# Revit family: IS_Ceraline_A6938_BIM_NL
name_source: partatom
category: Plumbing Fixtures
units: mm (PartAtom-declared; Revit-internal decimal feet)

## family parameters
Always vertical = No
Cut with Voids When Loaded = No
OmniClass Number = 23.45.55.17
OmniClass Title = Mixing Faucets
Part Type = Normal
Room Calculation Point = No
Round Connector Dimension = Use Diameter
Shared = No
Work Plane-Based = No

## types (2) — shared parameters
Accesoires = https://www.idealstandard.nl
Afmetingen = 113 x 213 x 193 mm
AfstandsEenheid = Millimeter
Artikelreferentie = CERALINE WASCHTISCHMISCHER EINBAUKIT2 HORIZ/A1313NU
Auteur = Ideal Standard
BIMObjectName = Washbasin manual water supply sets_Ceraline_A6938AA_Ideal Standard
BIMobject category = Sanitary
BIMobject category code = Sanitary Taps & Mixer
BIMobject main category = Sanitary
BIMobject main category code = sanitary
BOSUseNativeGeometries = 1
Bedieningkraan = Handbuch
Bedieningkraanwerk = einzelne Ebene
Beschrijvinggarantie = Herstellergarantie
BimObjectNaam = Washbasin manual water supply sets_Ceraline_A6938AA_Ideal Standard
Brand url = http://www.idealstandard.nl
Breedte = 193.000002
Date of publishing = 20/05/2019
Diepte = 213 mm  [stored 0.698819 ft]
DikteMateriaal = Messing
Doorstromingscoëfficiënt = 14L/min
Douchebak = No
DuurEenheid = Jaren
Edition number = 1
Features = CERALINE BSN MXR BIN KIT2 H/A5948NU MENA
Functiekraanwerk = Einhebelgriff
Garantieunits = Jaren
GemaaktOp = 22/07/2021
Hoogte = 113.464935302735
Hulp = https://www.idealstandard.nl
IFC Classification = Sanitary Terminal
IfcExportAs = IfcValveType
IfcExportType = FAUCED
Installatieinstructies = https://www.idealstandard.nl
Installation instructions = https://www.idealstandard.nl
Lengte = 213 mm  [stored 0.698819 ft]
Manufacturer name = Ideal Standard
Masterformat 2014 Code = 41 14 33
Masterformat 2014 Description = Mixer
Materiaal = Messing
Material main = Brass
Merk = Ideal Standard
ModelReference = CERALINE BSN MXR BIN KIT2 H/A5948NU MENA
Montageinstuctie = https://www.idealstandard.nl
NBS Reference Code = 45-35-70/371
NBS Reference Description = Washbasin manual water supply sets
Name = IS_IdealStandard_Washbasinmanualwatersupplysets_Ceraline_A6938AA
Nettogewicht = 0.88
NominalHeight = 113 mm
NominalLength = 213 mm  [stored 0.698819 ft]
NominalWidth = 193 mm
Normen = IS_IdealStandard_Washbasinmanualwatersupplysets_Ceraline_A6938AA
OmniClass Code = 23-31 11 00
OmniClass Description = Faucets
OppervlakteEenheid = Millimeter
Product Guid = 513090a8-e12e-4011-8710-158d55a47c0e
Product certification = https://www.idealstandard.nl
Product data url = https://bimobject.com
Product family = Ceraline
Product group = Washbasin manual water supply sets
Product name = CERALINE BSN MXR BIN KIT2 H/A5948NU MENA
Product url = https://www.idealstandard.nl
ProductSoort = Armaturen Mixer
Productinformatie = https://www.idealstandard.nl
QR code = http://bimobject.com
Referentie = CERALINE BSN MXR BIN KIT2 H/A5948NU MENA
Revisie = 1
Size = 113 x 213 x 193 mm
Technical description = https://www.idealstandard.nl
Telefoonnummer = 077 355 08 08
Testdruk = 10 Bar
Typeconnectie = Installation
URL = https://www.idealstandard.nl
Uniclass 2015 Code = Pr_40_20_87_96
Uniclass 2015 Name = Washbasin manual water supply sets
Urlproducent = https://www.idealstandard.nl
ValutaEenheid = Euro
Versie = 1
Volumeunits = Liter
Vorm = zylindrisch
WarrantyDescription = Manufacturers Warranty
WarrantyDurationParts = 5
WarrantyDurationUnit = year
Wisselstukken = https://www.idealstandard.nl
Youtube clip = https://www.youtube.com
zero-valued in all types: BrutoGewicht, Cost, Overloop, Vervangingskosten

## per-type parameters (varying)
| type | Afwerking | Artikelnummer | Artikelomschrijving | BarCode | Barcode | Description | Eigenschappen | Finish | GTIN code | Kleur | Model | ModelNumber | Product SKU | Uniclass 1.4 Code | Uniclass 1.4 Description | Uniclass2015Beschrijving | Uniclass2015Referentie | Uniclass2015Version |
| A6938AA - CERALINE BASIN MIXER BUILT-IN KIT2 HORIZ/A1313NU  - CHROME | chrom | A6938AA | CERALINE WASCHTISCHMISCHER EINBAUKIT2 HORIZ/A1313NU - CHROM | 4015413343879 | 4015413343879 | CERALINE BASIN MIXER BUILT-IN KIT2 HORIZ/A1313NU  - CHROME | WASCHTISCHMISCHER EINBAUKIT2 HORIZ/A1313NU - CHROM | chrom | https://4015413343879 | chrom | A6938AA | A6938AA | A6938AA |  |  |  |  |  |
| A6938XG - CERALINE BASIN MIXER BUILT-IN KIT2 HORIZ/A1313NU  - SILK BLACK | seide schwarz | A6938XG | CERALINE WASCHTISCHMISCHER EINBAUKIT2 HORIZ/A1313NU - SEIDE SCHWARZ | 4015413350884 | 4015413350884 | CERALINE BASIN MIXER BUILT-IN KIT2 HORIZ/A1313NU  - SILK BLACK | WASCHTISCHMISCHER EINBAUKIT2 HORIZ/A1313NU - SEIDE SCHWARZ | seide schwarz | https://4015413350884 | seide schwarz | A6938XG | A6938XG | A6938XG | L725111 | Mixers taps | Washbasin manual water supply sets | Pr_40_20_87_96 | v1.22 |

note: [stored X ft] marks values corroborated as IEEE doubles in the binary element streams (Revit-internal decimal feet)

## geometry (parser evidence)
native form markers: Sweep x3
no freeform markers — native parametric forms only
